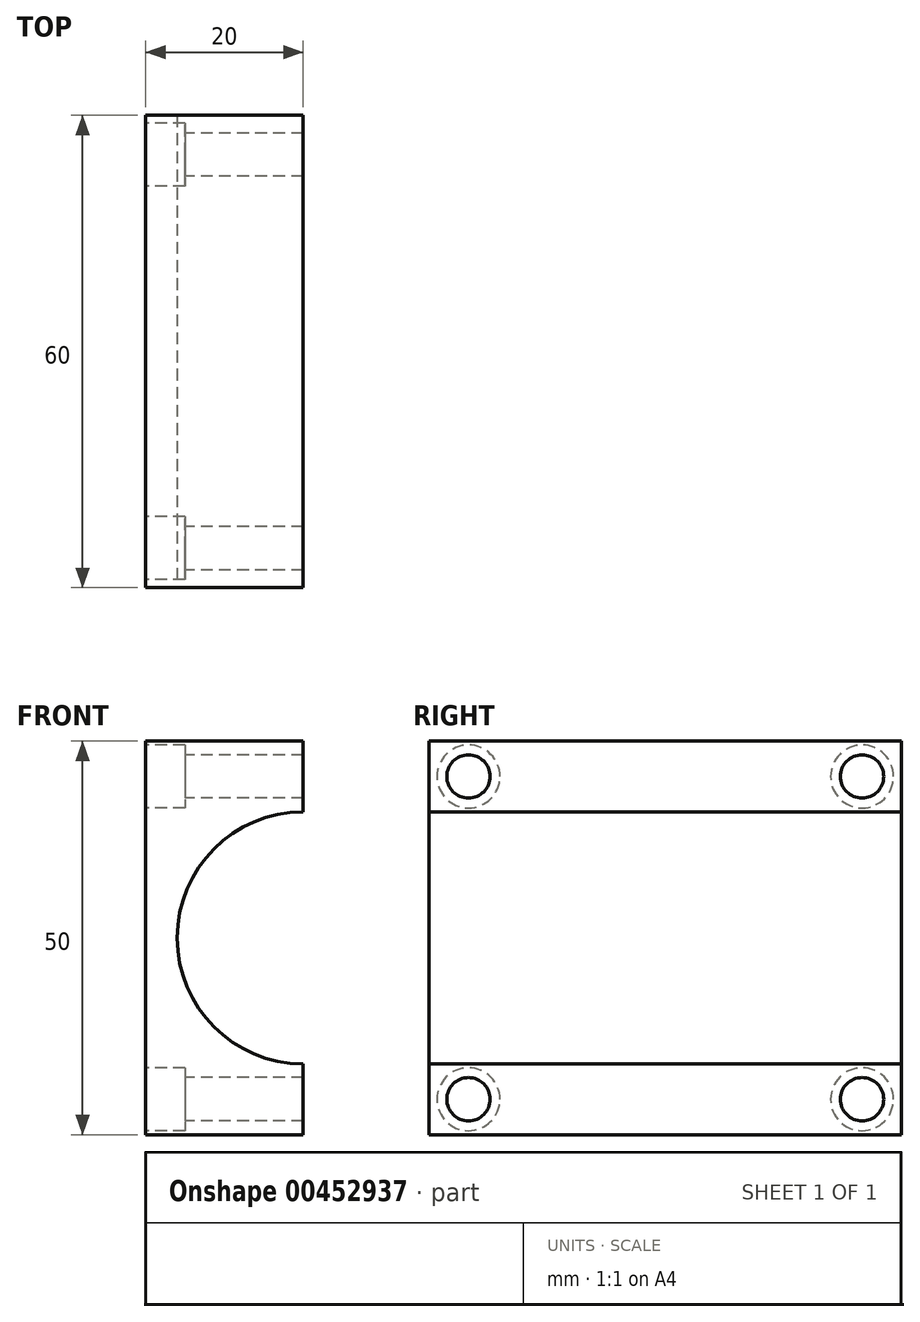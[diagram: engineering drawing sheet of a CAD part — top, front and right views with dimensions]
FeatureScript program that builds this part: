
annotation { "Feature Type Name" : "Feature", "Feature Type Description" : "" }
export const myFeature = defineFeature(function(context is Context, id is Id, definition is map)
    precondition{}
    {
        {
            var Q0;
            Q0=qCreatedBy(makeId("Right.planeOp"),FACE);
            var sketch = newSketch(context, id + "F0", { "sketchPlane" : qUnion([Q0])});
            skLineSegment(sketch, "E0.bottom", {"start": v(0, 0) * mm, "end": v(60, 0) * mm});
            skLineSegment(sketch, "E0.top", {"start": v(0, -50) * mm, "end": v(60, -50) * mm});
            skLineSegment(sketch, "E0.left", {"start": v(0, 0) * mm, "end": v(0, -50) * mm});
            skLineSegment(sketch, "E0.right", {"start": v(60, 0) * mm, "end": v(60, -50) * mm});
            skSolve(sketch);
        }
        {
            var Q0;
            Q0 = qSketchRegion(id + "F0", true);
            var sketch = newSketch(context, id + "F1", { "sketchPlane" : qUnion([Q0])});
            skSolve(sketch);
        }
        {
            var Q0;
            Q0 = qSketchRegion(id + "F0", true);
            var Q1;
            Q1=makeQuery(id+"F1.imprint","IMPRINT",FACE,{"disambiguationData":[TD([[makeQuery(id+"F1.imprint","IMPRINT",EDGE,{"derivedFrom":makeQuery(id+"F0.imprint","IMPRINT",EDGE,{"derivedFrom":sQuery(id+"F0.wireOp",EDGE,"E0.bottom")})}),-1.0]])]});
            extrude(context, id + "F2", {"entities" : qUnion([Q0, Q1]), "oppositeDirection" : true, "depth" : 40 * mm});
        }
        {
            var Q0;
            {var subQ0=sQuery(id+"F0.wireOp",EDGE,"E0.left");Q0=makeQuery(id+"F2.opExtrude","SWEPT_FACE",FACE,{"disambiguationData":[OSD([subQ0]),TDD([makeQuery(id+"F1.imprint","IMPRINT",EDGE,{"derivedFrom":makeQuery(id+"F0.imprint","IMPRINT",EDGE,{"derivedFrom":subQ0})})])]});}
            var sketch = newSketch(context, id + "F3", { "sketchPlane" : qUnion([Q0])});
            skCircle(sketch, "E1", {"center": v(-20, -25) * mm, "radius": 16 * mm});
            skSolve(sketch);
        }
        {
            var Q0;
            Q0=sQuery(id+"F3.wireOp",VERTEX,"E1.center");
            var Q1;
            {var subQ0=sQuery(id+"F0.wireOp",EDGE,"E0.right");var subQ1=sQuery(id+"F0.wireOp",EDGE,"E0.left");var subQ2=sQuery(id+"F0.wireOp",EDGE,"E0.top");var subQ3=sQuery(id+"F0.wireOp",EDGE,"E0.bottom");Q1=makeQuery(id+"F2.opExtrude","SWEPT_BODY",BODY,{"disambiguationData":[OSD([subQ3,subQ2,subQ1,subQ0]),TDD([makeQuery(id+"F0.imprint","IMPRINT",EDGE,{"derivedFrom":subQ3}),makeQuery(id+"F0.imprint","IMPRINT",EDGE,{"derivedFrom":subQ2}),makeQuery(id+"F0.imprint","IMPRINT",EDGE,{"derivedFrom":subQ1}),makeQuery(id+"F0.imprint","IMPRINT",EDGE,{"derivedFrom":subQ0})])]});}
            var Q2;
            {var subQ0=sQuery(id+"F0.wireOp",EDGE,"E0.right");var subQ1=sQuery(id+"F0.wireOp",EDGE,"E0.left");var subQ2=sQuery(id+"F0.wireOp",EDGE,"E0.top");var subQ3=sQuery(id+"F0.wireOp",EDGE,"E0.bottom");Q2=makeQuery(id+"F2.opExtrude","SWEPT_BODY",BODY,{"disambiguationData":[OSD([subQ3,subQ2,subQ1,subQ0]),TDD([makeQuery(id+"F1.imprint","IMPRINT",EDGE,{"derivedFrom":makeQuery(id+"F0.imprint","IMPRINT",EDGE,{"derivedFrom":subQ3})}),makeQuery(id+"F1.imprint","IMPRINT",EDGE,{"derivedFrom":makeQuery(id+"F0.imprint","IMPRINT",EDGE,{"derivedFrom":subQ2})}),makeQuery(id+"F1.imprint","IMPRINT",EDGE,{"derivedFrom":makeQuery(id+"F0.imprint","IMPRINT",EDGE,{"derivedFrom":subQ1})}),makeQuery(id+"F1.imprint","IMPRINT",EDGE,{"derivedFrom":makeQuery(id+"F0.imprint","IMPRINT",EDGE,{"derivedFrom":subQ0})})])]});}
            hole(context, id + "F4", {"style" : HoleStyle.SIMPLE, "endStyle" : HoleEndStyle.THROUGH, "holeDiameter" : 32 * mm, "isTappedThrough" : true, "tappedDepth" : 12 * mm, "tapClearance" : 3, "locations" : qUnion([Q0]), "scope" : qUnion([Q1, Q2])});
        }
        {
            var Q0;
            Q0=makeQuery(id+"F0.imprint","IMPRINT",FACE,{"disambiguationData":[TD([[makeQuery(id+"F0.imprint","IMPRINT",EDGE,{"derivedFrom":sQuery(id+"F0.wireOp",EDGE,"E0.bottom")}),-1.0]])]});
            var sketch = newSketch(context, id + "F5", { "sketchPlane" : qUnion([Q0])});
            skLineSegment(sketch, "E2.bottom", {"start": v(0, 0) * mm, "end": v(60, 0) * mm});
            skLineSegment(sketch, "E2.top", {"start": v(0, -50) * mm, "end": v(60, -50) * mm});
            skLineSegment(sketch, "E2.left", {"start": v(0, 0) * mm, "end": v(0, -50) * mm});
            skLineSegment(sketch, "E2.right", {"start": v(60, 0) * mm, "end": v(60, -50) * mm});
            skSolve(sketch);
        }
        {
            var Q0;
            Q0=makeQuery(id+"F5.imprint","IMPRINT",FACE,{"disambiguationData":[TD([[makeQuery(id+"F5.imprint","IMPRINT",EDGE,{"derivedFrom":sQuery(id+"F5.wireOp",EDGE,"E2.bottom")}),-1.0]])]});
            extrude(context, id + "F6", {"entities" : qUnion([Q0]), "operationType" : NewBodyOperationType.REMOVE, "oppositeDirection" : true, "depth" : 20 * mm});
        }
        {
            var Q0;
            {var subQ0=sQuery(id+"F0.wireOp",EDGE,"E0.right");var subQ1=sQuery(id+"F0.wireOp",EDGE,"E0.left");var subQ2=sQuery(id+"F0.wireOp",EDGE,"E0.top");var subQ3=sQuery(id+"F0.wireOp",EDGE,"E0.bottom");Q0=makeQuery(id+"F2.opExtrude","CAP_FACE",FACE,{"disambiguationData":[OSD([subQ3,subQ2,subQ1,subQ0]),TDD([makeQuery(id+"F0.imprint","IMPRINT",EDGE,{"derivedFrom":subQ3}),makeQuery(id+"F0.imprint","IMPRINT",EDGE,{"derivedFrom":subQ2}),makeQuery(id+"F0.imprint","IMPRINT",EDGE,{"derivedFrom":subQ1}),makeQuery(id+"F0.imprint","IMPRINT",EDGE,{"derivedFrom":subQ0})])],"isStart":false});}
            var sketch = newSketch(context, id + "F7", { "sketchPlane" : qUnion([Q0])});
            skCircle(sketch, "E3", {"center": v(-55, -4.5) * mm, "radius": 2.56 * mm});
            skCircle(sketch, "E4", {"center": v(-5, -4.5) * mm, "radius": 2.39 * mm});
            skSolve(sketch);
        }
        {
            var Q0;
            Q0=makeQuery(id+"F7.imprint","IMPRINT",FACE,{"disambiguationData":[TD([[makeQuery(id+"F7.imprint","IMPRINT",EDGE,{"derivedFrom":sQuery(id+"F7.wireOp",EDGE,"E3")}),-1.0]])]});
            var sketch = newSketch(context, id + "F8", { "sketchPlane" : qUnion([Q0])});
            skCircle(sketch, "E5", {"center": v(-55, -45.5) * mm, "radius": 2.1 * mm});
            skCircle(sketch, "E6", {"center": v(-5, -45.5) * mm, "radius": 2.1 * mm});
            skSolve(sketch);
        }
        {
            var Q0;
            Q0=sQuery(id+"F7.wireOp",VERTEX,"E3.center");
            var Q1;
            Q1=sQuery(id+"F7.wireOp",VERTEX,"E4.center");
            var Q2;
            Q2=sQuery(id+"F8.wireOp",VERTEX,"E6.center");
            var Q3;
            Q3=sQuery(id+"F8.wireOp",VERTEX,"E5.center");
            var Q4;
            {var subQ0=sQuery(id+"F0.wireOp",EDGE,"E0.right");var subQ1=sQuery(id+"F0.wireOp",EDGE,"E0.left");var subQ2=sQuery(id+"F0.wireOp",EDGE,"E0.top");var subQ3=sQuery(id+"F0.wireOp",EDGE,"E0.bottom");Q4=makeQuery(id+"F2.opExtrude","SWEPT_BODY",BODY,{"disambiguationData":[OSD([subQ3,subQ2,subQ1,subQ0]),TDD([makeQuery(id+"F0.imprint","IMPRINT",EDGE,{"derivedFrom":subQ3}),makeQuery(id+"F0.imprint","IMPRINT",EDGE,{"derivedFrom":subQ2}),makeQuery(id+"F0.imprint","IMPRINT",EDGE,{"derivedFrom":subQ1}),makeQuery(id+"F0.imprint","IMPRINT",EDGE,{"derivedFrom":subQ0})])]});}
            var Q5;
            {var subQ0=sQuery(id+"F0.wireOp",EDGE,"E0.right");var subQ1=sQuery(id+"F0.wireOp",EDGE,"E0.left");var subQ2=sQuery(id+"F0.wireOp",EDGE,"E0.top");var subQ3=sQuery(id+"F0.wireOp",EDGE,"E0.bottom");Q5=makeQuery(id+"F2.opExtrude","SWEPT_BODY",BODY,{"disambiguationData":[OSD([subQ3,subQ2,subQ1,subQ0]),TDD([makeQuery(id+"F1.imprint","IMPRINT",EDGE,{"derivedFrom":makeQuery(id+"F0.imprint","IMPRINT",EDGE,{"derivedFrom":subQ3})}),makeQuery(id+"F1.imprint","IMPRINT",EDGE,{"derivedFrom":makeQuery(id+"F0.imprint","IMPRINT",EDGE,{"derivedFrom":subQ2})}),makeQuery(id+"F1.imprint","IMPRINT",EDGE,{"derivedFrom":makeQuery(id+"F0.imprint","IMPRINT",EDGE,{"derivedFrom":subQ1})}),makeQuery(id+"F1.imprint","IMPRINT",EDGE,{"derivedFrom":makeQuery(id+"F0.imprint","IMPRINT",EDGE,{"derivedFrom":subQ0})})])]});}
            hole(context, id + "F9", {"style" : HoleStyle.C_BORE, "endStyle" : HoleEndStyle.THROUGH, "holeDiameter" : 5.5 * mm, "cBoreDiameter" : 8 * mm, "cBoreDepth" : 5 * mm, "isTappedThrough" : true, "tappedDepth" : 12 * mm, "tapClearance" : 3, "locations" : qUnion([Q0, Q1, Q2, Q3]), "scope" : qUnion([Q4, Q5])});
        }
    });
